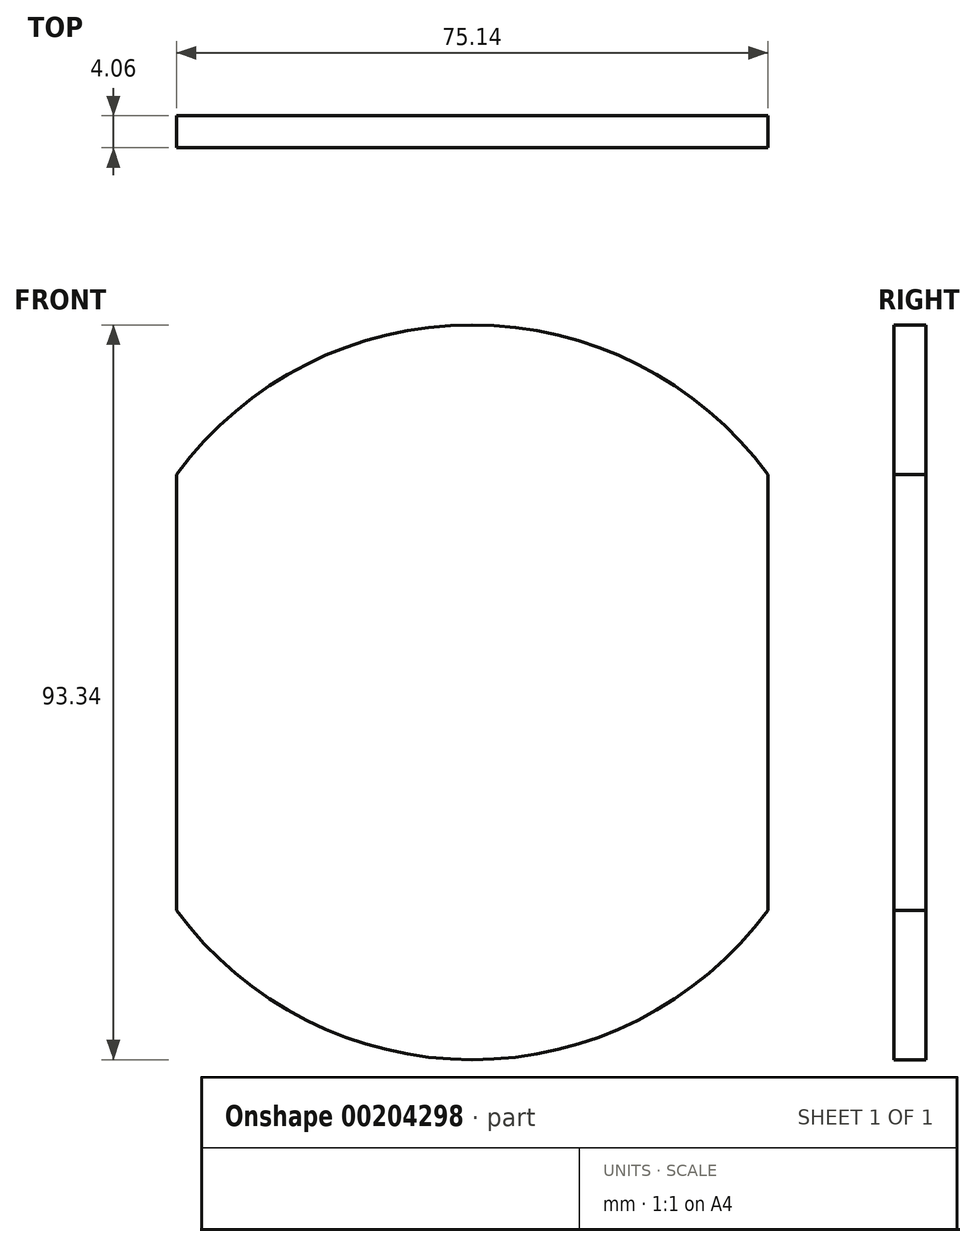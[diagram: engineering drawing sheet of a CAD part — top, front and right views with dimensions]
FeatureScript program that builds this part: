
annotation { "Feature Type Name" : "Feature", "Feature Type Description" : "" }
export const myFeature = defineFeature(function(context is Context, id is Id, definition is map)
    precondition{}
    {
        {
            var Q0;
            Q0=qCreatedBy(makeId("Front.planeOp"),FACE);
            var sketch = newSketch(context, id + "F0", { "sketchPlane" : qUnion([Q0])});
            skArc(sketch, "E0", {"start": v(-37.57, -27.7) * mm, "mid": v(0, -46.67) * mm, "end": v(37.57, -27.7) * mm});
            skLineSegment(sketch, "E1", {"start": v(-37.57, 27.7) * mm, "end": v(-37.57, -27.7) * mm});
            skLineSegment(sketch, "E2.MirrorCS", {"start": v(37.57, 27.7) * mm, "end": v(37.57, -27.7) * mm});
            skArc(sketch, "E3.trimOffspring", {"start": v(37.57, 27.7) * mm, "mid": v(0, 46.67) * mm, "end": v(-37.57, 27.7) * mm});
            skSolve(sketch);
        }
        {
            var Q0;
            Q0=makeQuery(id+"F0.imprint","IMPRINT",FACE,{"disambiguationData":[TD([[makeQuery(id+"F0.imprint","IMPRINT",EDGE,{"derivedFrom":sQuery(id+"F0.wireOp",EDGE,"E0")}),1.0]])]});
            extrude(context, id + "F1", {"entities" : qUnion([Q0]), "oppositeDirection" : true, "depth" : 4.06 * mm});
        }
    });
